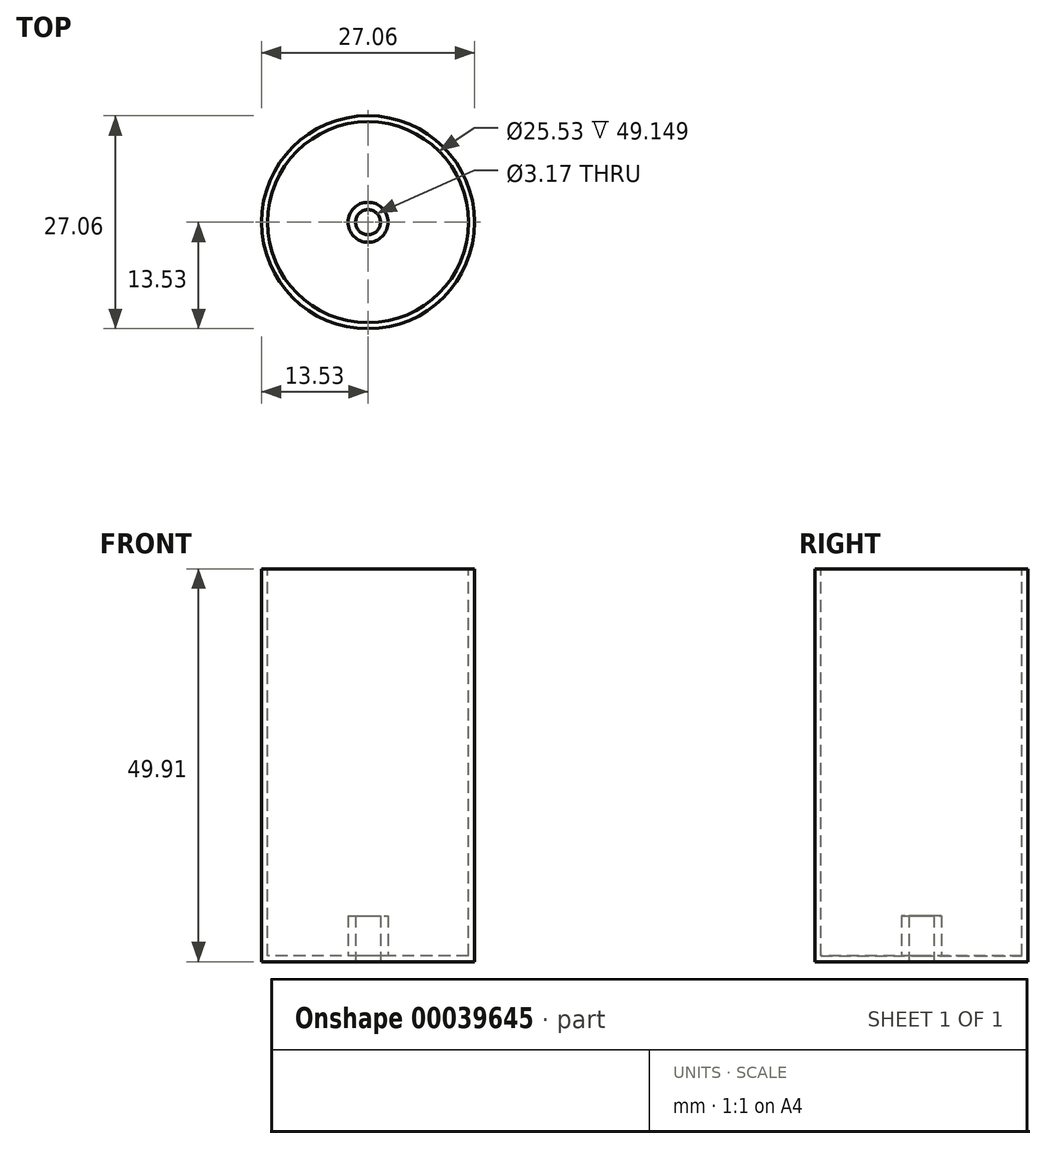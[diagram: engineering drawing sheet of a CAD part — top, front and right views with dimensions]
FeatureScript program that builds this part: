
annotation { "Feature Type Name" : "Feature", "Feature Type Description" : "" }
export const myFeature = defineFeature(function(context is Context, id is Id, definition is map)
    precondition{}
    {
        {
            var Q0;
            Q0=qCreatedBy(makeId("Top.planeOp"),FACE);
            var sketch = newSketch(context, id + "F0", { "sketchPlane" : qUnion([Q0])});
            skCircle(sketch, "E0", {"center": v(0, 0) * mm, "radius": 13.53 * mm});
            skSolve(sketch);
        }
        {
            var Q0;
            Q0=makeQuery(id+"F0.imprint","IMPRINT",FACE,{"disambiguationData":[TD([[makeQuery(id+"F0.imprint","IMPRINT",EDGE,{"derivedFrom":sQuery(id+"F0.wireOp",EDGE,"E0")}),1.0]])]});
            extrude(context, id + "F1", {"entities" : qUnion([Q0]), "oppositeDirection" : true, "depth" : 49.9 * mm});
        }
        {
            var Q0;
            Q0=makeQuery(id+"F1.opExtrude","CAP_FACE",FACE,{"disambiguationData":[OSD([sQuery(id+"F0.wireOp",EDGE,"E0")])],"isStart":true});
            var sketch = newSketch(context, id + "F2", { "sketchPlane" : qUnion([Q0])});
            skCircle(sketch, "E1", {"center": v(0, 0) * mm, "radius": 12.76 * mm});
            skSolve(sketch);
        }
        {
            var Q0;
            Q0 = qSketchRegion(id + "F2", true);
            extrude(context, id + "F3", {"entities" : qUnion([Q0]), "operationType" : NewBodyOperationType.REMOVE, "oppositeDirection" : true, "depth" : 49.15 * mm});
        }
        {
            var Q0;
            Q0=makeQuery(id+"F1.opExtrude","CAP_FACE",FACE,{"disambiguationData":[OSD([sQuery(id+"F0.wireOp",EDGE,"E0")])],"isStart":false});
            var sketch = newSketch(context, id + "F4", { "sketchPlane" : qUnion([Q0])});
            skCircle(sketch, "E2", {"center": v(0, 0) * mm, "radius": 2.54 * mm});
            skCircle(sketch, "E3", {"center": v(0, 0) * mm, "radius": 1.59 * mm});
            skSolve(sketch);
        }
        {
            var Q0;
            Q0 = qSketchRegion(id + "F4", true);
            extrude(context, id + "F5", {"entities" : qUnion([Q0]), "operationType" : NewBodyOperationType.ADD, "oppositeDirection" : true, "depth" : 5.84 * mm});
        }
        {
            var Q0;
            Q0=makeQuery(id+"F1.opExtrude","CAP_FACE",FACE,{"disambiguationData":[OSD([sQuery(id+"F0.wireOp",EDGE,"E0")])],"isStart":false});
            var sketch = newSketch(context, id + "F6", { "sketchPlane" : qUnion([Q0])});
            skCircle(sketch, "E4", {"center": v(0, 0) * mm, "radius": 1.59 * mm});
            skSolve(sketch);
        }
        {
            var Q0;
            Q0 = qSketchRegion(id + "F6", true);
            extrude(context, id + "F7", {"entities" : qUnion([Q0]), "operationType" : NewBodyOperationType.REMOVE, "endBound" : BoundingType.THROUGH_ALL, "oppositeDirection" : true, "depth" : 25.4 * mm});
        }
    });
